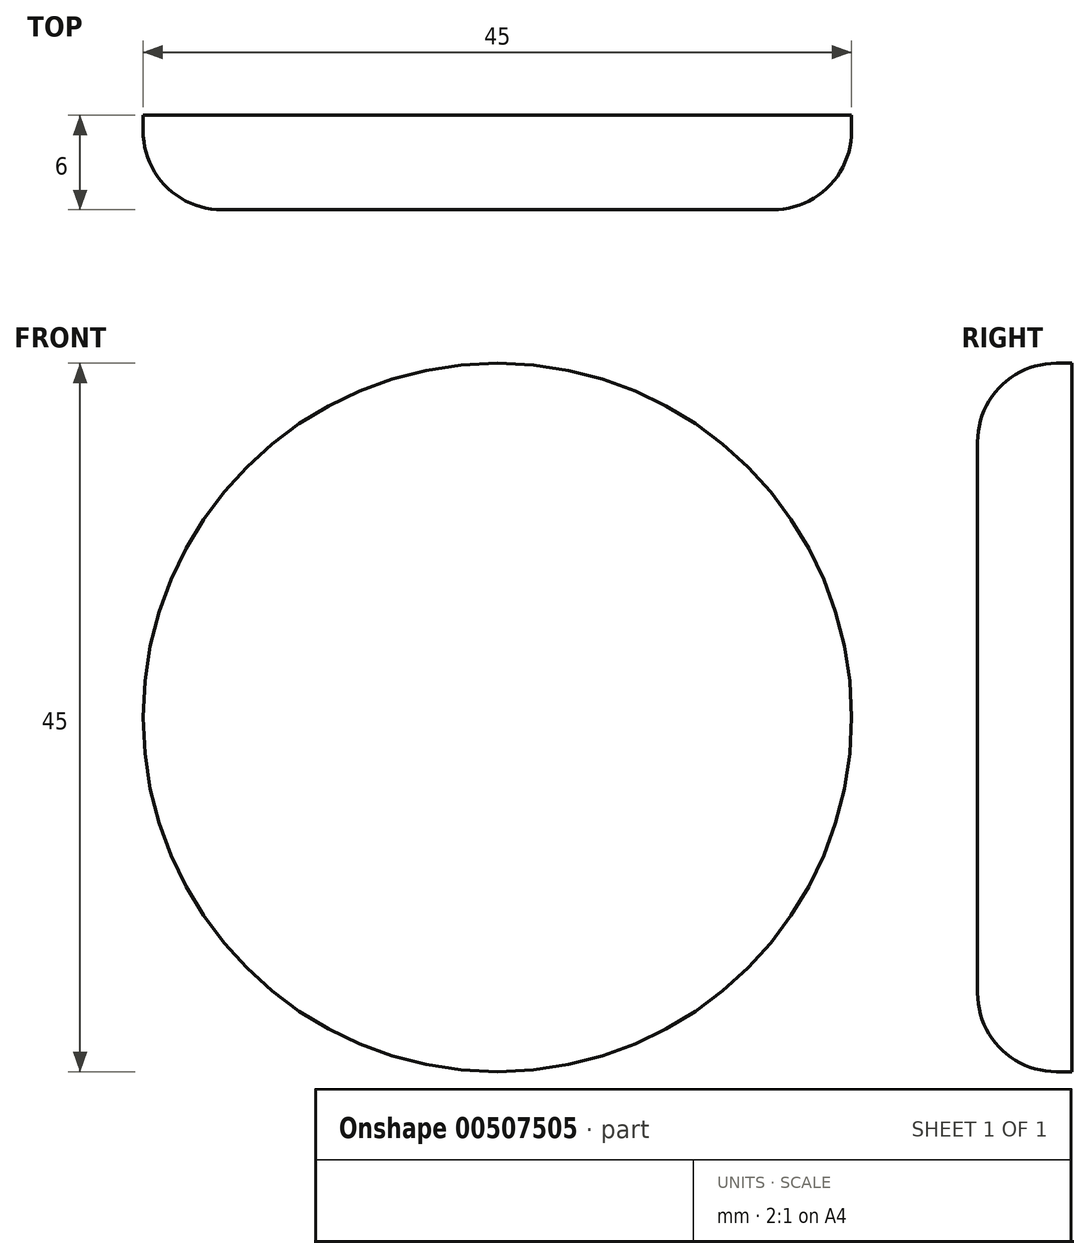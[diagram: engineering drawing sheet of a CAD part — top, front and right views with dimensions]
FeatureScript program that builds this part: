
annotation { "Feature Type Name" : "Feature", "Feature Type Description" : "" }
export const myFeature = defineFeature(function(context is Context, id is Id, definition is map)
    precondition{}
    {
        {
            var Q0;
            Q0=qCreatedBy(makeId("Front.planeOp"),FACE);
            var sketch = newSketch(context, id + "F0", { "sketchPlane" : qUnion([Q0])});
            skCircle(sketch, "E0", {"center": v(0, 0) * mm, "radius": 22.5 * mm});
            skSolve(sketch);
        }
        {
            var Q0;
            Q0 = qSketchRegion(id + "F0", true);
            extrude(context, id + "F1", {"entities" : qUnion([Q0]), "depth" : 6 * mm});
        }
        {
            var Q0;
            Q0=makeQuery(id+"F1.opExtrude","CAP_EDGE",EDGE,{"disambiguationData":[OSD([sQuery(id+"F0.wireOp",EDGE,"E0")])],"isStart":false});
            fillet(context, id + "F2", {"entities" : qUnion([Q0]), "radius" : 5 * mm, "allowEdgeOverflow" : false});
        }
    });
